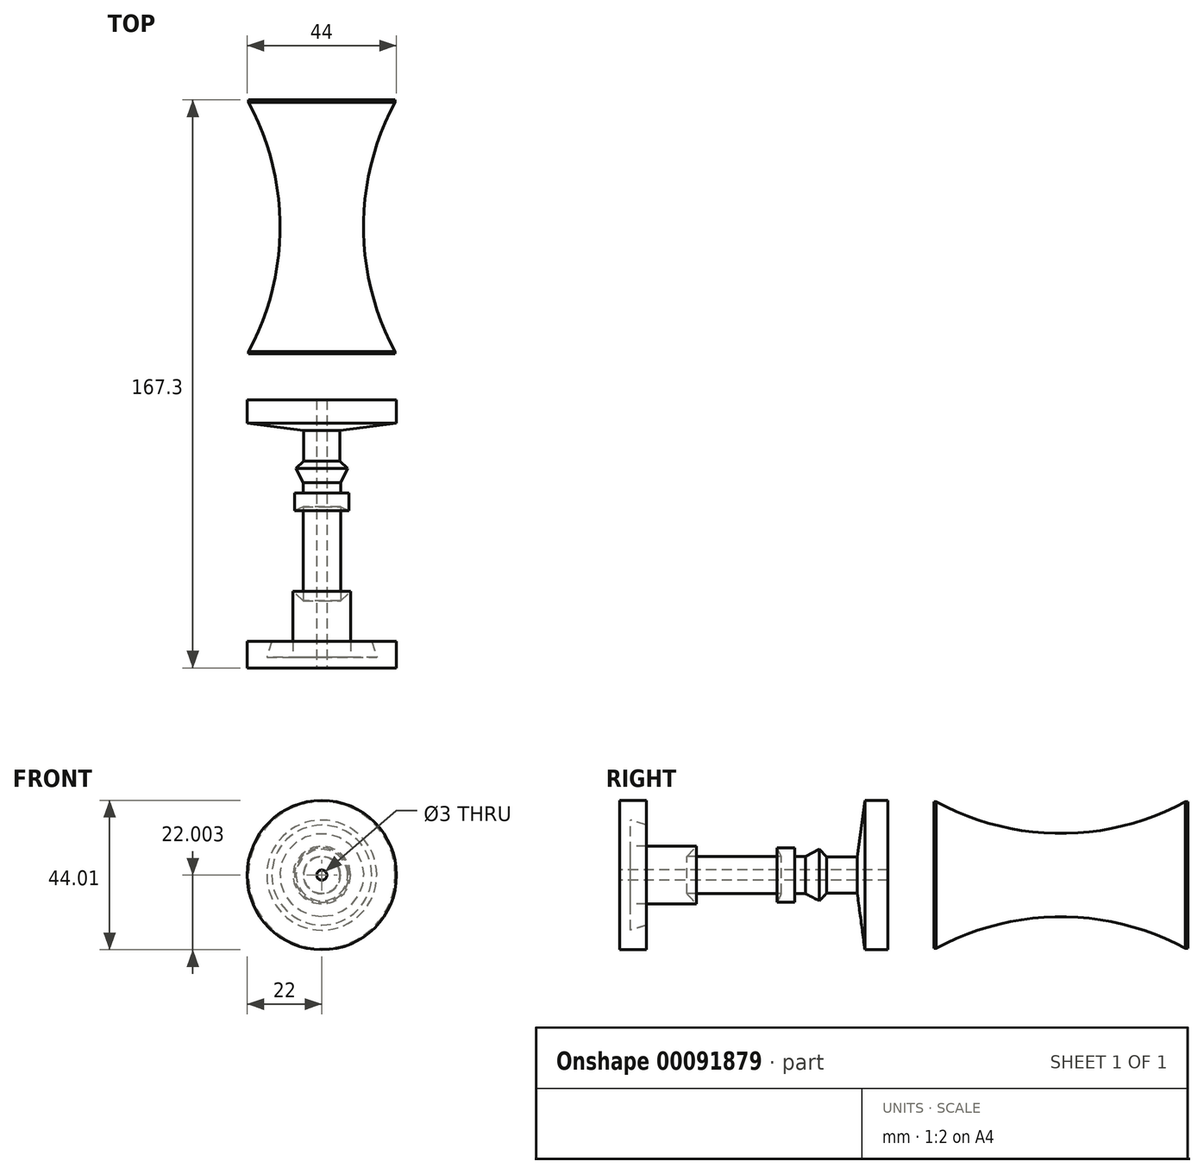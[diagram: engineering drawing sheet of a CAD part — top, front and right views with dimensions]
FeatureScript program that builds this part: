
annotation { "Feature Type Name" : "Feature", "Feature Type Description" : "" }
export const myFeature = defineFeature(function(context is Context, id is Id, definition is map)
    precondition{}
    {
        {
            var Q0;
            Q0=qCreatedBy(makeId("Right.planeOp"),FACE);
            var sketch = newSketch(context, id + "F0", { "sketchPlane" : qUnion([Q0])});
            skLineSegment(sketch, "E0", {"start": v(-31.43, -4.48) * mm, "end": v(47.24, -4.48) * mm});
            skLineSegment(sketch, "E1", {"start": v(-32.1, 0) * mm, "end": v(-32.1, 20.5) * mm});
            skLineSegment(sketch, "E2", {"start": v(-32.1, 20.5) * mm, "end": v(46.9, 20.5) * mm});
            skLineSegment(sketch, "E3", {"start": v(46.9, 20.5) * mm, "end": v(46.9, 0) * mm});
            skLineSegment(sketch, "E4", {"start": v(46.9, 0) * mm, "end": v(40.07, 0) * mm});
            skLineSegment(sketch, "E5", {"start": v(40.07, 0) * mm, "end": v(37.84, 16.64) * mm});
            skLineSegment(sketch, "E6", {"start": v(37.84, 16.64) * mm, "end": v(28.79, 16.64) * mm});
            skLineSegment(sketch, "E7", {"start": v(28.79, 16.64) * mm, "end": v(26.7, 14.42) * mm});
            skLineSegment(sketch, "E8", {"start": v(26.7, 14.42) * mm, "end": v(22.55, 16.5) * mm});
            skLineSegment(sketch, "E9", {"start": v(22.55, 16.5) * mm, "end": v(19.43, 16.5) * mm});
            skLineSegment(sketch, "E10", {"start": v(19.43, 16.5) * mm, "end": v(19.43, 13.97) * mm});
            skLineSegment(sketch, "E11", {"start": v(19.43, 13.97) * mm, "end": v(14.23, 13.97) * mm});
            skLineSegment(sketch, "E12", {"start": v(14.23, 13.97) * mm, "end": v(15.42, 16.5) * mm});
            skLineSegment(sketch, "E13", {"start": v(15.42, 16.5) * mm, "end": v(-12.35, 16.5) * mm});
            skLineSegment(sketch, "E14", {"start": v(-12.35, 16.5) * mm, "end": v(-9.52, 13.53) * mm});
            skLineSegment(sketch, "E15", {"start": v(-9.52, 13.53) * mm, "end": v(-28.98, 13.53) * mm});
            skLineSegment(sketch, "E16", {"start": v(-28.98, 13.53) * mm, "end": v(-28.98, 5.8) * mm});
            skLineSegment(sketch, "E17", {"start": v(-28.98, 5.8) * mm, "end": v(-24.22, 7.29) * mm});
            skLineSegment(sketch, "E18", {"start": v(-24.22, 7.29) * mm, "end": v(-24.22, 0) * mm});
            skLineSegment(sketch, "E19", {"start": v(-24.22, 0) * mm, "end": v(-32.1, 0) * mm});
            skArc(sketch, "E20", {"start": v(135.21, 0) * mm, "mid": v(97.81, 9.72) * mm, "end": v(60.41, 0) * mm});
            skLineSegment(sketch, "E21.left", {"start": v(60.41, 0) * mm, "end": v(60.41, 0) * mm});
            skLineSegment(sketch, "E21.right", {"start": v(135.21, 0) * mm, "end": v(135.21, 0) * mm});
            skLineSegment(sketch, "E22.bottom", {"start": v(60.41, 0) * mm, "end": v(60.03, 0) * mm});
            skLineSegment(sketch, "E22.top", {"start": v(135.21, 0.39) * mm, "end": v(134.51, 0.39) * mm});
            skLineSegment(sketch, "E22.left", {"start": v(135.21, 0) * mm, "end": v(135.21, 0.39) * mm});
            skLineSegment(sketch, "E22.right", {"start": v(60.03, 0) * mm, "end": v(60.03, 0.39) * mm});
            skLineSegment(sketch, "E23.bottom", {"start": v(60.41, 22) * mm, "end": v(135.21, 22) * mm});
            skLineSegment(sketch, "E23.top", {"start": v(60.41, 0.39) * mm, "end": v(61.11, 0.39) * mm});
            skLineSegment(sketch, "E23.left", {"start": v(60.41, 22) * mm, "end": v(60.41, 0.39) * mm});
            skLineSegment(sketch, "E23.right", {"start": v(135.21, 22) * mm, "end": v(135.21, 0.39) * mm});
            skLineSegment(sketch, "E24.trimOffspring", {"start": v(61.11, 0.39) * mm, "end": v(60.03, 0.39) * mm});
            skLineSegment(sketch, "E25.trimOffspring", {"start": v(134.51, 0.39) * mm, "end": v(135.21, 0.39) * mm});
            skSolve(sketch);
        }
        {
            var Q0;
            Q0=makeQuery(id+"F0.imprint","IMPRINT",FACE,{"disambiguationData":[TD([[makeQuery(id+"F0.imprint","IMPRINT",EDGE,{"derivedFrom":sQuery(id+"F0.wireOp",EDGE,"E1")}),-1.0]])]});
            var Q1;
            Q1=makeQuery(id+"F0.imprint","IMPRINT",FACE,{"disambiguationData":[TD([[makeQuery(id+"F0.imprint","IMPRINT",EDGE,{"derivedFrom":sQuery(id+"F0.wireOp",EDGE,"E23.bottom")}),-1.0]])]});
            var Q2;
            Q2=sQuery(id+"F0.wireOp",EDGE,"E23.bottom");
            revolve(context, id + "F1", {"entities" : qUnion([Q0, Q1]), "axis" : qUnion([Q2]), "revolveType" : RevolveType.FULL});
        }
    });
